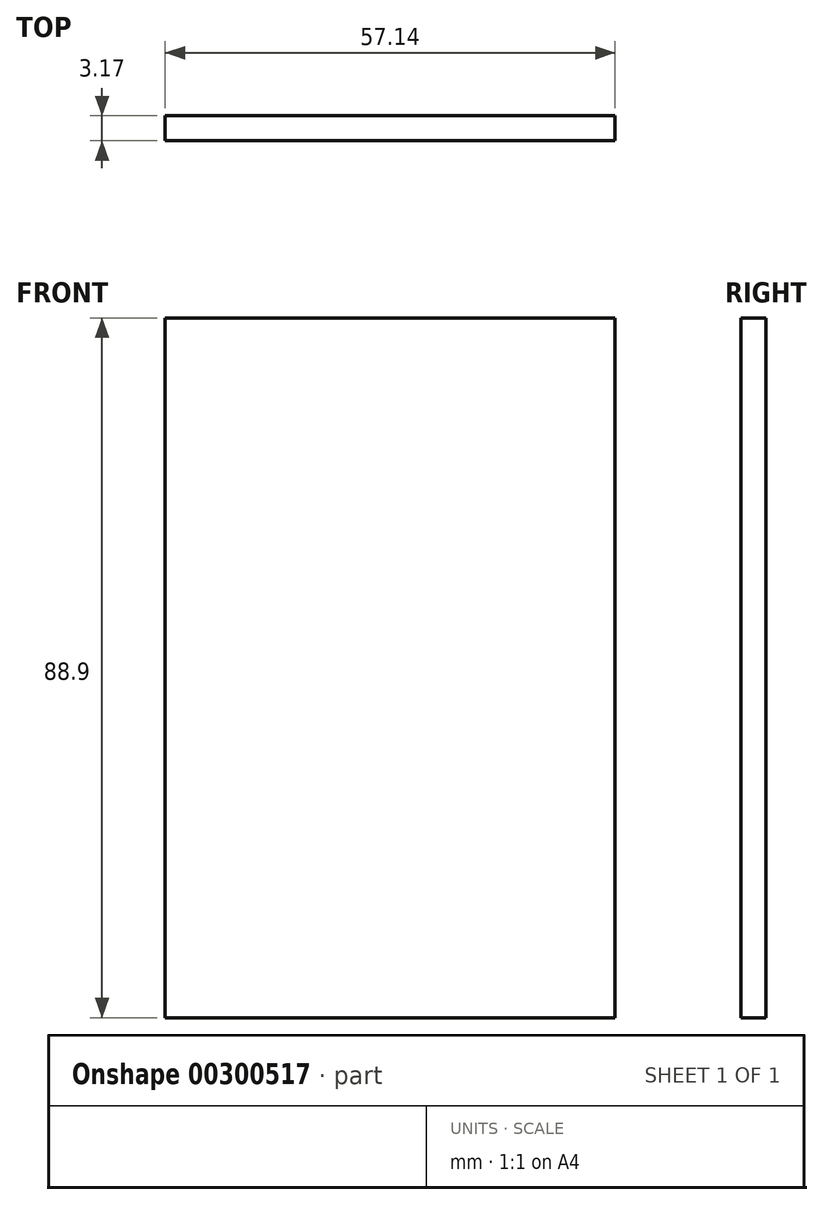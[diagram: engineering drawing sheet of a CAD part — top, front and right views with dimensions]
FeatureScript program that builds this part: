
annotation { "Feature Type Name" : "Feature", "Feature Type Description" : "" }
export const myFeature = defineFeature(function(context is Context, id is Id, definition is map)
    precondition{}
    {
        {
            var Q0;
            Q0=qCreatedBy(makeId("Front.planeOp"),FACE);
            var sketch = newSketch(context, id + "F0", { "sketchPlane" : qUnion([Q0])});
            skLineSegment(sketch, "E0.bottom", {"start": v(28.57, 44.45) * mm, "end": v(-28.58, 44.45) * mm});
            skLineSegment(sketch, "E0.top", {"start": v(28.58, -44.45) * mm, "end": v(-28.57, -44.45) * mm});
            skLineSegment(sketch, "E0.left", {"start": v(28.57, 44.45) * mm, "end": v(28.58, -44.45) * mm});
            skLineSegment(sketch, "E0.right", {"start": v(-28.58, 44.45) * mm, "end": v(-28.57, -44.45) * mm});
            skPoint(sketch, "E0.middle", {"position": v(0, 0) * mm});
            skSolve(sketch);
        }
        {
            var Q0;
            Q0 = qSketchRegion(id + "F0", true);
            extrude(context, id + "F1", {"entities" : qUnion([Q0]), "depth" : 3.17 * mm});
        }
    });
